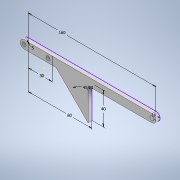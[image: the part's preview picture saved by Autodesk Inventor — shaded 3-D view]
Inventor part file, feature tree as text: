
AUTODESK INVENTOR PART (.ipt)
format: ipt  version: 2022 (Build 260153000, 153)  size: 117,760 bytes
history: native  units: mm
features: extrude x3, sketch x1
ambient origin geometry x8: Origin, YZ Plane, XZ Plane, XY Plane, X Axis, Y Axis, Z Axis, Center Point
bodies: Solid1 (feature_tree)
feature tree (4):
  sketch  "Sketch1"  dims[d0=10.0mm d1=5.0mm d2=160.0mm d3=5.0mm d4=0.0mm d7=30.0mm d8=10.0mm d9=0.0mm d10=45.0deg d11=40.0mm d12=80.0mm d13=10.0mm d14=0.0mm]
  extrude  "Extrusion1"  Depth=5.0mm
  extrude  "Extrusion3"  Depth=10.0mm
  extrude  "Extrusion4"  Depth=5.0mm TaperAngle=0.0deg
